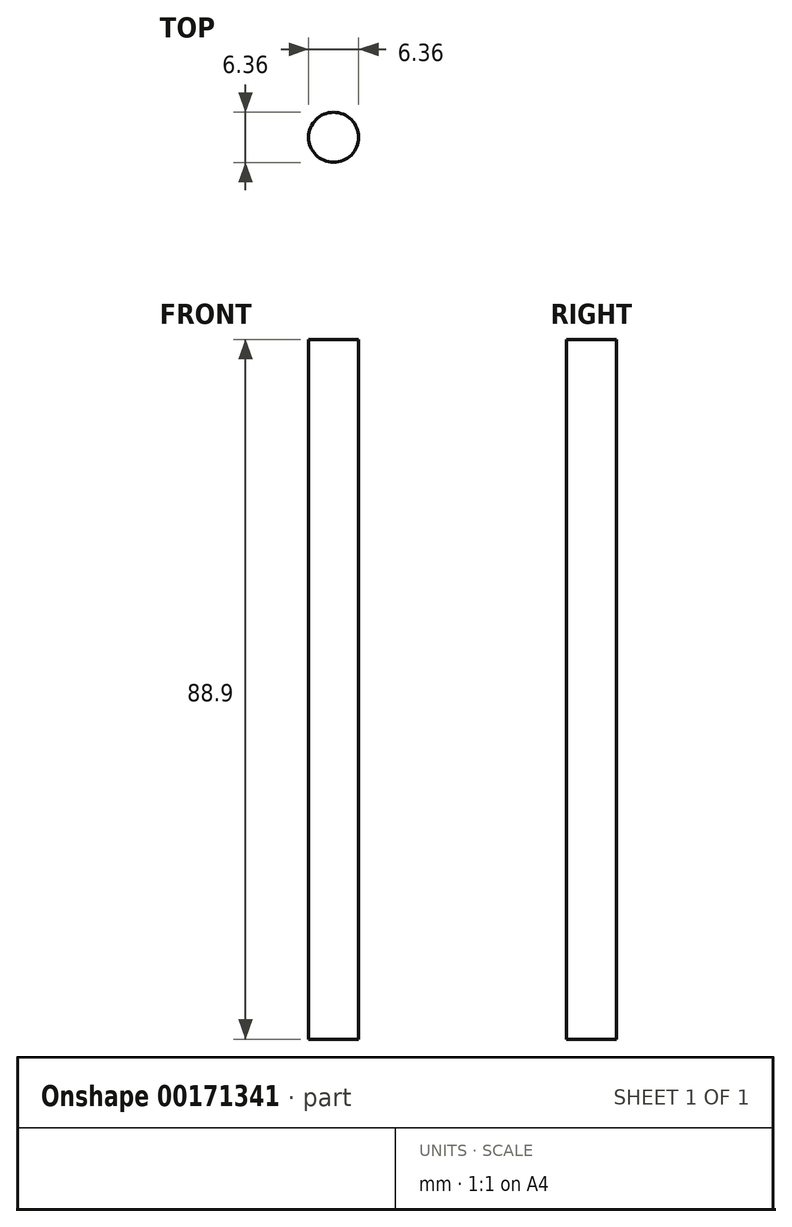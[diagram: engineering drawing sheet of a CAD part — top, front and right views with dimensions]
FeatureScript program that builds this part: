
annotation { "Feature Type Name" : "Feature", "Feature Type Description" : "" }
export const myFeature = defineFeature(function(context is Context, id is Id, definition is map)
    precondition{}
    {
        {
            var Q0;
            Q0=qCreatedBy(makeId("Top.planeOp"),FACE);
            var sketch = newSketch(context, id + "F0", { "sketchPlane" : qUnion([Q0])});
            skCircle(sketch, "E0", {"center": v(0, 0) * mm, "radius": 3.18 * mm});
            skSolve(sketch);
        }
        {
            var Q0;
            Q0=makeQuery(id+"F0.imprint","IMPRINT",FACE,{"disambiguationData":[TD([[makeQuery(id+"F0.imprint","IMPRINT",EDGE,{"derivedFrom":sQuery(id+"F0.wireOp",EDGE,"E0")}),1.0]])]});
            extrude(context, id + "F1", {"entities" : qUnion([Q0]), "depth" : 88.9 * mm});
        }
    });
